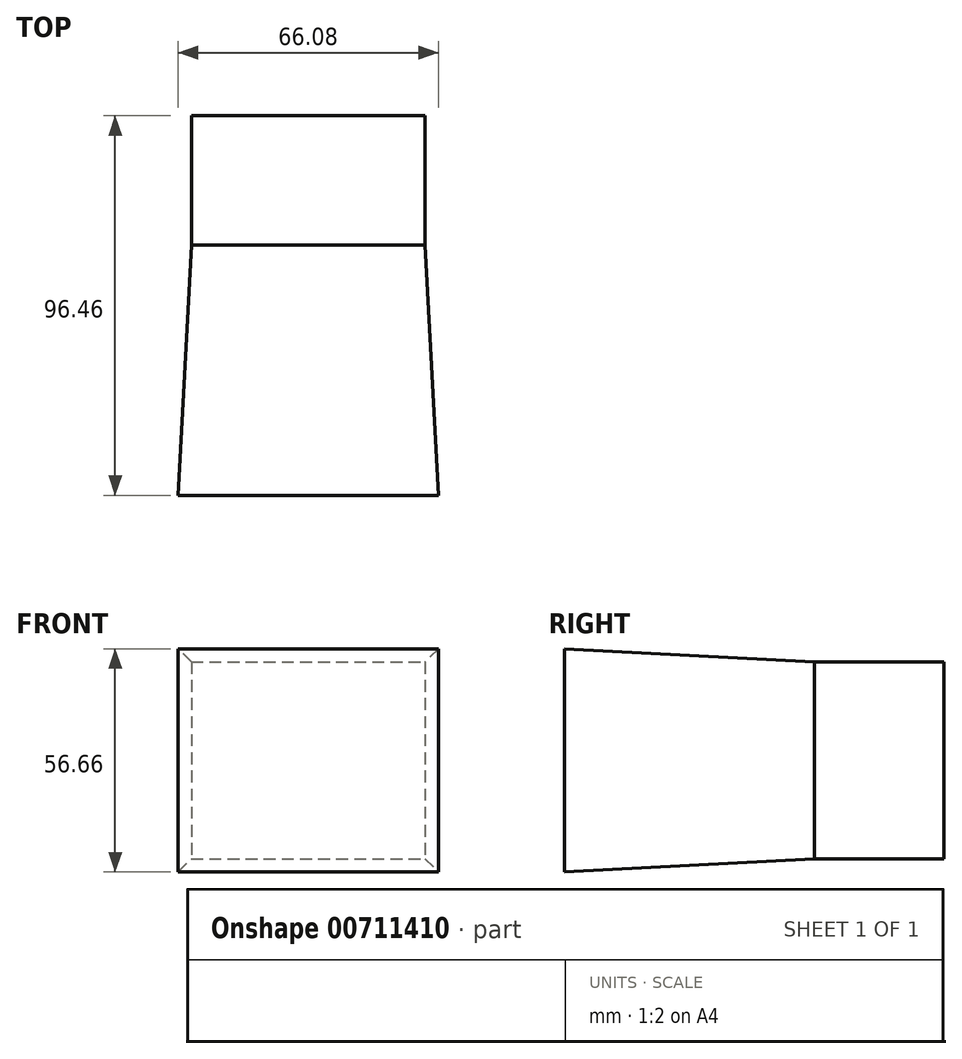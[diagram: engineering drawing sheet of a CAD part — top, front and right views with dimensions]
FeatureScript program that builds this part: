
annotation { "Feature Type Name" : "Feature", "Feature Type Description" : "" }
export const myFeature = defineFeature(function(context is Context, id is Id, definition is map)
    precondition{}
    {
        {
            var Q0;
            Q0=qCreatedBy(makeId("Top.planeOp"),FACE);
            var sketch = newSketch(context, id + "F0", { "sketchPlane" : qUnion([Q0])});
            skLineSegment(sketch, "E0.bottom", {"start": v(0, 0) * mm, "end": v(59.42, 0) * mm});
            skLineSegment(sketch, "E0.top", {"start": v(0, -32.87) * mm, "end": v(59.42, -32.87) * mm});
            skLineSegment(sketch, "E0.left", {"start": v(0, 0) * mm, "end": v(0, -32.87) * mm});
            skLineSegment(sketch, "E0.right", {"start": v(59.42, 0) * mm, "end": v(59.42, -32.87) * mm});
            skSolve(sketch);
        }
        {
            var Q0;
            Q0=makeQuery(id+"F0.imprint","IMPRINT",FACE,{"disambiguationData":[TD([[makeQuery(id+"F0.imprint","IMPRINT",EDGE,{"derivedFrom":sQuery(id+"F0.wireOp",EDGE,"E0.bottom")}),-1.0]])]});
            extrude(context, id + "F1", {"entities" : qUnion([Q0]), "depth" : 50 * mm, "offsetDistance" : 25 * mm});
        }
        {
            var Q0;
            Q0=makeQuery(id+"F1.opExtrude","SWEPT_FACE",FACE,{"disambiguationData":[OSD([sQuery(id+"F0.wireOp",EDGE,"E0.top")])]});
            extrude(context, id + "F2", {"entities" : qUnion([Q0]), "operationType" : NewBodyOperationType.ADD, "depth" : 63.58 * mm, "offsetDistance" : 25 * mm, "hasDraft" : true, "draftAngle" : 0.05 * radian});
        }
    });
